# Revit family: Haworth_ActiveComponents_WedgeFullConvergent
name_source: partatom
category: Furniture Systems
revit_build: Autodesk Revit 2018 (Build: 20170223_1515(x64)
units: mm (PartAtom-declared; Revit-internal decimal feet)

## family parameters
Always vertical = Yes
Cut with Voids When Loaded = No
OmniClass Number = 23.40.70.14.64.21
OmniClass Title = Systems Furniture
Part Type = Normal
Room Calculation Point = No
Round Connector Dimension = Use Diameter
Shared = No
Work Plane-Based = No

## types (2) — shared parameters
Actual Height = 29 3/16"
Assembly Code = E2020200
Description = Haworth - Active Components - Wedge Full Convergent
Inside Radius = 1 1/2"
Leg Back Offset = 8 1/8"
Leg L/R Offset = 3 9/16"
Manufacturer = Haworth
Max. Depth = 36"
Max. Width = 72"
Min. Depth = 34"
Min. Width = 60"
Model = WAYP
Narrow Depth = 24"
Radius = 3 1/2"
Revision Number = 1
Size = Verify Final Dim. w/ Haworth
Surface Angle = 10.00°
Thickness = 1 3/16"
URL = www.haworth.com
URL - Product = https://www.haworth.com
Warranty = https://www.haworth.com
With Leg = Yes

## per-type parameters (varying)
| type | Actual Depth | Actual Width | Depth | Leg Front Offset | Width |
| 36d 72w | 36" | 72" | 36" | 20 1/8" | 72" |
| 34d 60w | 34" | 60" | 34" | 18 1/8" | 60" |

## geometry (parser evidence)
native form markers: Sweep x9
no freeform markers — native parametric forms only
